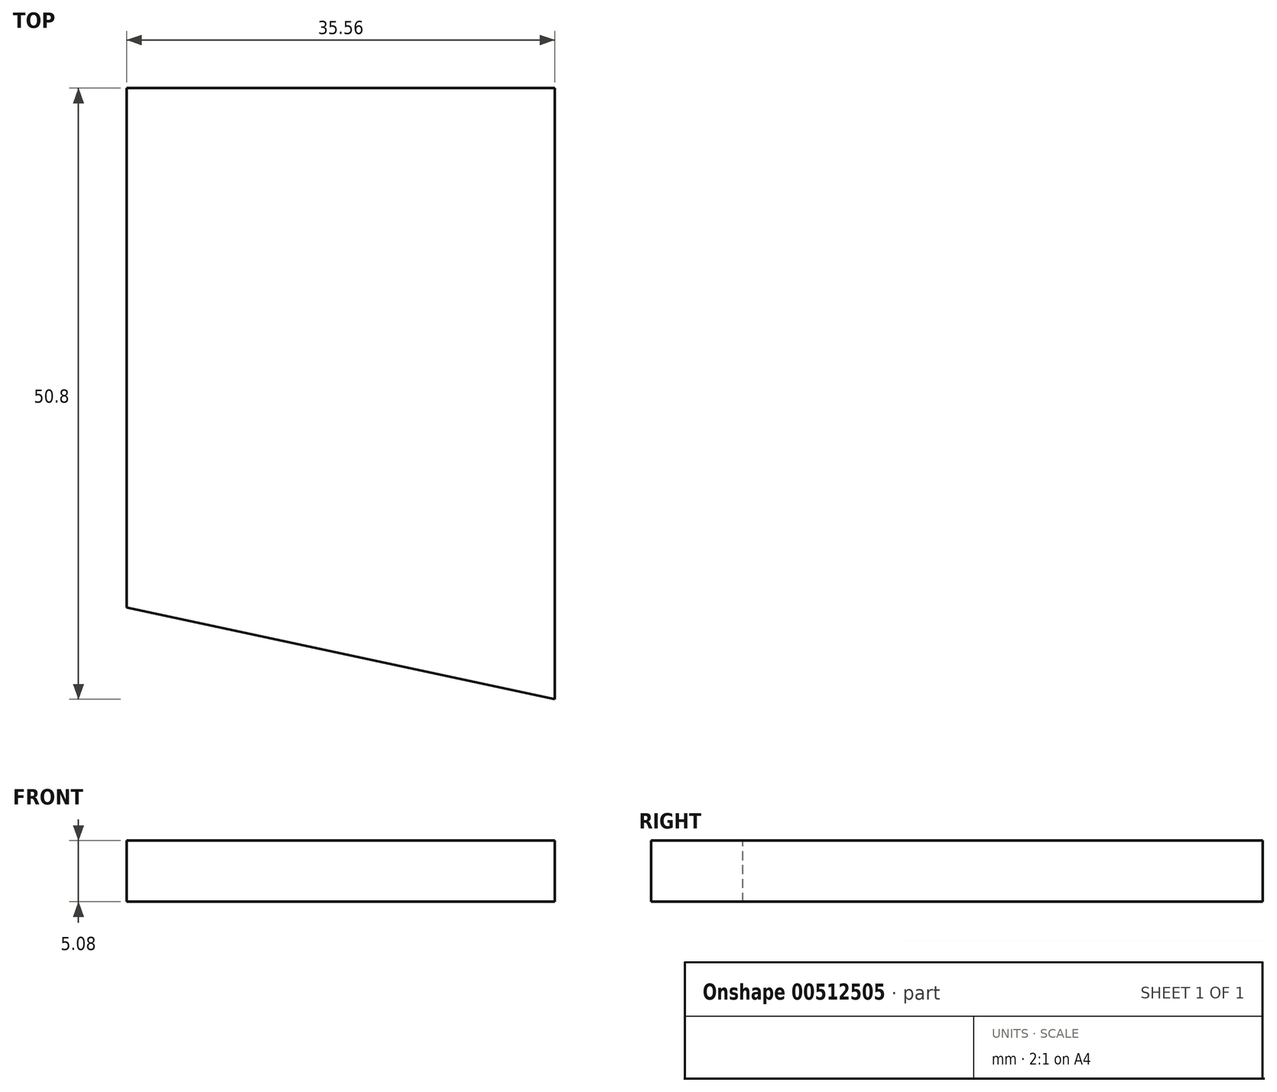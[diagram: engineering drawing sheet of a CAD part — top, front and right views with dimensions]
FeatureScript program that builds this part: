
annotation { "Feature Type Name" : "Feature", "Feature Type Description" : "" }
export const myFeature = defineFeature(function(context is Context, id is Id, definition is map)
    precondition{}
    {
        {
            var Q0;
            Q0=qCreatedBy(makeId("Top.planeOp"),FACE);
            var sketch = newSketch(context, id + "F0", { "sketchPlane" : qUnion([Q0])});
            skLineSegment(sketch, "E0.bottom", {"start": v(-37.06, -28.6) * mm, "end": v(-1.5, -28.6) * mm});
            skLineSegment(sketch, "E0.top", {"start": v(-37.06, 22.2) * mm, "end": v(-1.5, 22.2) * mm});
            skLineSegment(sketch, "E0.left", {"start": v(-37.06, -28.6) * mm, "end": v(-37.06, 22.2) * mm});
            skLineSegment(sketch, "E0.right", {"start": v(-1.5, -28.6) * mm, "end": v(-1.5, 22.2) * mm});
            skSolve(sketch);
        }
        {
            var Q0;
            Q0=makeQuery(id+"F0.imprint","IMPRINT",FACE,{"disambiguationData":[TD([[makeQuery(id+"F0.imprint","IMPRINT",EDGE,{"derivedFrom":sQuery(id+"F0.wireOp",EDGE,"E0.bottom")}),1.0]])]});
            extrude(context, id + "F1", {"entities" : qUnion([Q0]), "depth" : 5.08 * mm});
        }
        {
            var Q0;
            Q0=makeQuery(id+"F1.opExtrude","CAP_FACE",FACE,{"disambiguationData":[OSD([sQuery(id+"F0.wireOp",EDGE,"E0.bottom"),sQuery(id+"F0.wireOp",EDGE,"E0.top"),sQuery(id+"F0.wireOp",EDGE,"E0.left"),sQuery(id+"F0.wireOp",EDGE,"E0.right")])],"isStart":false});
            var sketch = newSketch(context, id + "F2", { "sketchPlane" : qUnion([Q0])});
            skLineSegment(sketch, "E1", {"start": v(-1.5, -28.6) * mm, "end": v(-37.06, -20.97) * mm});
            skSolve(sketch);
        }
        {
            var Q0;
            {var subQ0=sQuery(id+"F2.wireOp",EDGE,"E1");Q0=makeQuery(id+"F2.imprint","IMPRINT",FACE,{"disambiguationData":[TD([[makeQuery(id+"F2.imprint","IMPRINT",EDGE,{"derivedFrom":subQ0}),1.0]])]});}
            extrude(context, id + "F3", {"entities" : qUnion([Q0]), "operationType" : NewBodyOperationType.REMOVE, "oppositeDirection" : true, "depth" : 25.4 * mm, "offsetDistance" : 25.4 * mm});
        }
    });
